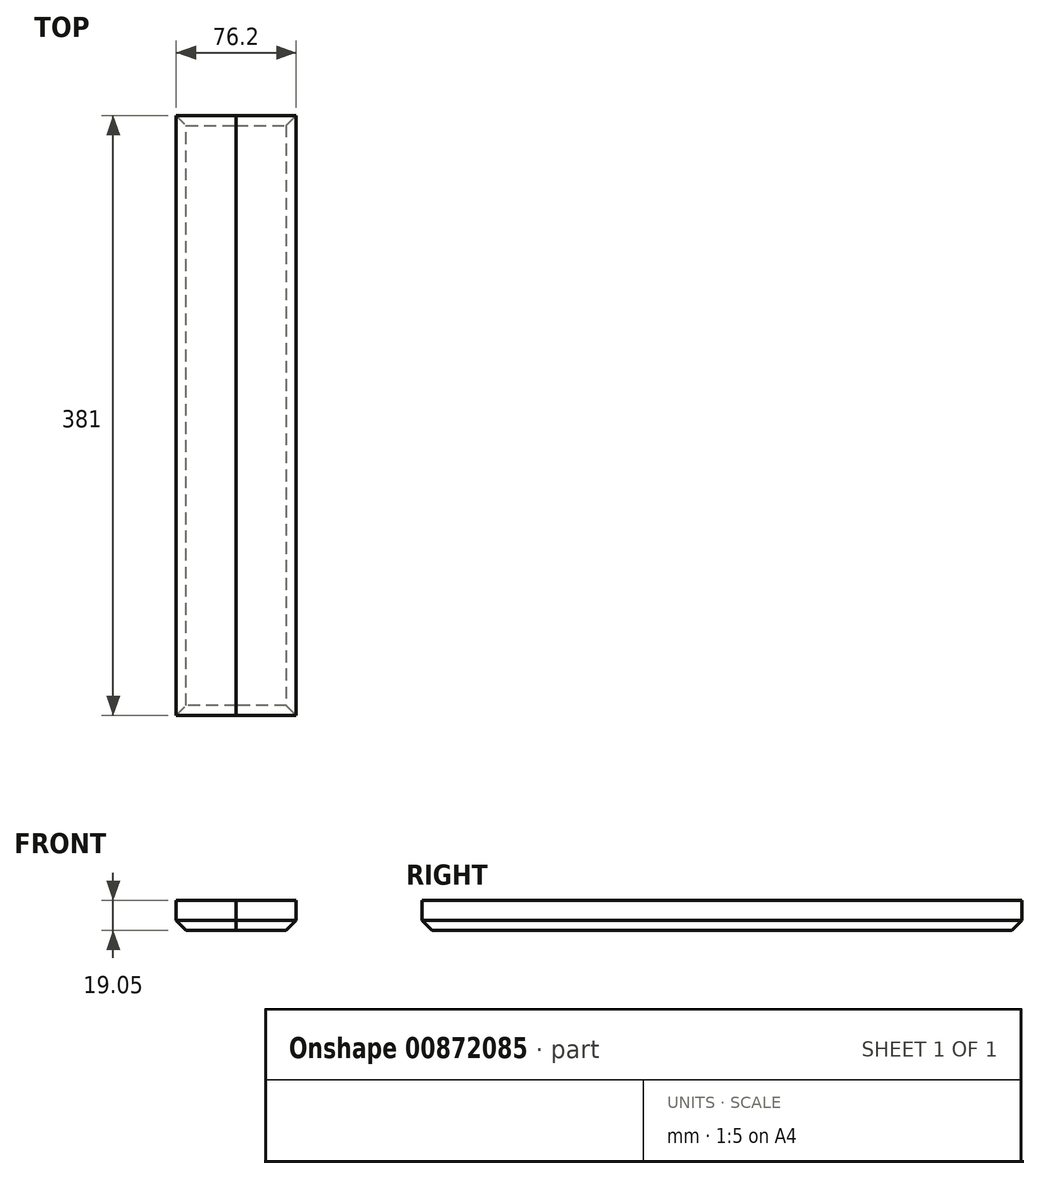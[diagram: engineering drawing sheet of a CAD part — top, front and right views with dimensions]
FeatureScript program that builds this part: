
annotation { "Feature Type Name" : "Feature", "Feature Type Description" : "" }
export const myFeature = defineFeature(function(context is Context, id is Id, definition is map)
    precondition{}
    {
        {
            var Q0;
            Q0=qCreatedBy(makeId("Front.planeOp"),FACE);
            var sketch = newSketch(context, id + "F0", { "sketchPlane" : qUnion([Q0])});
            skLineSegment(sketch, "E0.bottom", {"start": v(0, 0) * mm, "end": v(38.1, 0) * mm});
            skLineSegment(sketch, "E0.top", {"start": v(0, 19.05) * mm, "end": v(38.1, 19.05) * mm});
            skLineSegment(sketch, "E0.left", {"start": v(0, 0) * mm, "end": v(0, 19.05) * mm});
            skLineSegment(sketch, "E0.right", {"start": v(38.1, 0) * mm, "end": v(38.1, 19.05) * mm});
            skSolve(sketch);
        }
        {
            var Q0;
            Q0=qSketchRegion(id+"F0",true);
            extrude(context, id + "F1", {"entities" : qUnion([Q0]), "depth" : 381 * mm});
        }
        {
            var Q0;
            Q0=makeQuery(id+"F1.opExtrude","SWEPT_FACE",FACE,{"disambiguationData":[OSD([sQuery(id+"F0.wireOp",EDGE,"E0.top")])]});
            var sketch = newSketch(context, id + "F2", { "sketchPlane" : qUnion([Q0])});
            skLineSegment(sketch, "E1.bottom", {"start": v(38.1, 0) * mm, "end": v(76.2, 0) * mm});
            skLineSegment(sketch, "E1.top", {"start": v(38.1, -381) * mm, "end": v(76.2, -381) * mm});
            skLineSegment(sketch, "E1.left", {"start": v(38.1, 0) * mm, "end": v(38.1, -381) * mm});
            skLineSegment(sketch, "E1.right", {"start": v(76.2, 0) * mm, "end": v(76.2, -381) * mm});
            skSolve(sketch);
        }
        {
            var Q0;
            Q0=qSketchRegion(id+"F2",true);
            extrude(context, id + "F3", {"entities" : qUnion([Q0]), "depth" : -19.05 * mm});
        }
        {
            var Q0;
            Q0=makeQuery(id+"F1.opExtrude","SWEPT_EDGE",EDGE,{"disambiguationData":[OSD([sQuery(id+"F0.wireOp",EDGE,"E0.bottom"),sQuery(id+"F0.wireOp",EDGE,"E0.left")])]});
            var Q1;
            Q1=makeQuery(id+"F3.opExtrude","CAP_EDGE",EDGE,{"disambiguationData":[OSD([sQuery(id+"F2.wireOp",EDGE,"E1.right")])],"isStart":false});
            var Q2;
            Q2=makeQuery(id+"F3.opExtrude","CAP_EDGE",EDGE,{"disambiguationData":[OSD([sQuery(id+"F2.wireOp",EDGE,"E1.top")])],"isStart":false});
            var Q3;
            Q3=makeQuery(id+"F1.opExtrude","CAP_EDGE",EDGE,{"disambiguationData":[OSD([sQuery(id+"F0.wireOp",EDGE,"E0.bottom")])],"isStart":false});
            var Q4;
            Q4=makeQuery(id+"F3.opExtrude","CAP_EDGE",EDGE,{"disambiguationData":[OSD([sQuery(id+"F2.wireOp",EDGE,"E1.bottom")])],"isStart":false});
            var Q5;
            Q5=makeQuery(id+"F1.opExtrude","CAP_EDGE",EDGE,{"disambiguationData":[OSD([sQuery(id+"F0.wireOp",EDGE,"E0.bottom")])],"isStart":true});
            chamfer(context, id + "F4", {"entities" : qUnion([Q0, Q1, Q2, Q3, Q4, Q5]), "width" : 6.35 * mm, "tangentPropagation" : true});
        }
    });
